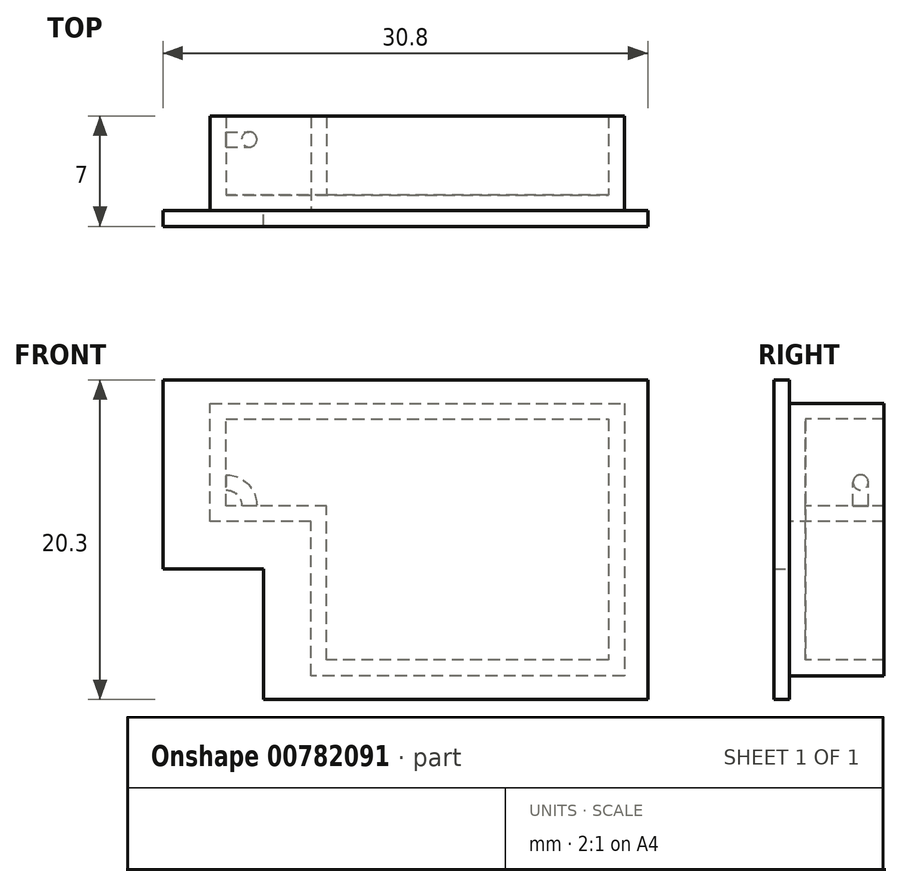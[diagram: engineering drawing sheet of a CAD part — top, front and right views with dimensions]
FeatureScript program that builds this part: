
annotation { "Feature Type Name" : "Feature", "Feature Type Description" : "" }
export const myFeature = defineFeature(function(context is Context, id is Id, definition is map)
    precondition{}
    {
        {
            var Q0;
            Q0=qCreatedBy(makeId("Front.planeOp"),FACE);
            var sketch = newSketch(context, id + "F0", { "sketchPlane" : qUnion([Q0])});
            skLineSegment(sketch, "E0", {"start": v(0, 0) * mm, "end": v(-19.9, 0) * mm});
            skLineSegment(sketch, "E1", {"start": v(-19.9, 0) * mm, "end": v(-19.9, 9.8) * mm});
            skLineSegment(sketch, "E2", {"start": v(-19.9, 9.8) * mm, "end": v(-26.3, 9.8) * mm});
            skLineSegment(sketch, "E3", {"start": v(-26.3, 9.8) * mm, "end": v(-26.3, 17.3) * mm});
            skLineSegment(sketch, "E4", {"start": v(-26.3, 17.3) * mm, "end": v(0, 17.3) * mm});
            skLineSegment(sketch, "E5", {"start": v(0, 17.3) * mm, "end": v(0, 0) * mm});
            skSolve(sketch);
        }
        {
            var Q0;
            Q0 = qSketchRegion(id + "F0", true);
            extrude(context, id + "F1", {"entities" : qUnion([Q0]), "oppositeDirection" : true, "depth" : 6 * mm, "offsetDistance" : 25 * mm});
        }
        {
            var Q0;
            Q0=makeQuery(id+"F1.opExtrude","CAP_FACE",FACE,{"disambiguationData":[OSD([sQuery(id+"F0.wireOp",EDGE,"E0"),sQuery(id+"F0.wireOp",EDGE,"E1"),sQuery(id+"F0.wireOp",EDGE,"E2"),sQuery(id+"F0.wireOp",EDGE,"E3"),sQuery(id+"F0.wireOp",EDGE,"E4"),sQuery(id+"F0.wireOp",EDGE,"E5")])],"isStart":false});
            shell(context, id + "F2", {"entities" : qUnion([Q0]), "thickness" : 1 * mm});
        }
        {
            var Q0;
            Q0=makeQuery(id+"F2.opShell","OFFSET_FACE",FACE,{"disambiguationData":[OSD([sQuery(id+"F0.wireOp",EDGE,"E2")])]});
            var sketch = newSketch(context, id + "F3", { "sketchPlane" : qUnion([Q0])});
            skCircle(sketch, "E6", {"center": v(-23.82, 4.52) * mm, "radius": 0.48 * mm});
            skLineSegment(sketch, "E7", {"start": v(-23.82, 5) * mm, "end": v(-23.82, 6) * mm, "construction": true});
            skLineSegment(sketch, "E8", {"start": v(-24.3, 4.52) * mm, "end": v(-25.3, 4.52) * mm, "construction": true});
            skSolve(sketch);
        }
        {
            var Q0;
            Q0 = qSketchRegion(id + "F3", true);
            var Q1;
            Q1=makeQuery(id+"F2.opShell","OFFSET_EDGE",EDGE,{"disambiguationData":[OSD([sQuery(id+"F0.wireOp",EDGE,"E2"),sQuery(id+"F0.wireOp",EDGE,"E3")])]});
            revolve(context, id + "F4", {"operationType" : NewBodyOperationType.ADD, "surfaceOperationType" : NewSurfaceOperationType.NEW, "entities" : qUnion([Q0]), "axis" : qUnion([Q1]), "revolveType" : RevolveType.ONE_DIRECTION, "angle" : 90 * degree});
        }
        {
            var Q0;
            Q0=makeQuery(id+"F1.opExtrude","CAP_FACE",FACE,{"disambiguationData":[OSD([sQuery(id+"F0.wireOp",EDGE,"E0"),sQuery(id+"F0.wireOp",EDGE,"E1"),sQuery(id+"F0.wireOp",EDGE,"E2"),sQuery(id+"F0.wireOp",EDGE,"E3"),sQuery(id+"F0.wireOp",EDGE,"E4"),sQuery(id+"F0.wireOp",EDGE,"E5")])],"isStart":true});
            var sketch = newSketch(context, id + "F5", { "sketchPlane" : qUnion([Q0])});
            skLineSegment(sketch, "E9", {"start": v(-26.3, 13.55) * mm, "end": v(-29.3, 13.55) * mm, "construction": true});
            skLineSegment(sketch, "E10", {"start": v(-13.15, 17.3) * mm, "end": v(-13.15, 18.8) * mm, "construction": true});
            skPoint(sketch, "E10.endSnap0", {"position": v(-13.15, 17.3) * mm});
            skLineSegment(sketch, "E11", {"start": v(0, 8.65) * mm, "end": v(1.5, 8.65) * mm, "construction": true});
            skPoint(sketch, "E11.endSnap0", {"position": v(0, 8.65) * mm});
            skLineSegment(sketch, "E12", {"start": v(-9.95, 0) * mm, "end": v(-9.95, -1.5) * mm, "construction": true});
            skPoint(sketch, "E12.endSnap0", {"position": v(-9.95, 0) * mm});
            skLineSegment(sketch, "E13", {"start": v(-19.9, 4.9) * mm, "end": v(-22.9, 4.9) * mm, "construction": true});
            skLineSegment(sketch, "E14", {"start": v(-25.21, 9.8) * mm, "end": v(-25.21, 6.8) * mm, "construction": true});
            skLineSegment(sketch, "E15", {"start": v(-29.3, 13.55) * mm, "end": v(-29.3, 18.8) * mm});
            skLineSegment(sketch, "E16", {"start": v(-29.3, 18.8) * mm, "end": v(1.5, 18.8) * mm});
            skLineSegment(sketch, "E17", {"start": v(1.5, 18.8) * mm, "end": v(1.5, -1.5) * mm});
            skLineSegment(sketch, "E18", {"start": v(1.5, -1.5) * mm, "end": v(-22.9, -1.5) * mm});
            skLineSegment(sketch, "E19", {"start": v(-22.9, -1.5) * mm, "end": v(-22.9, 4.9) * mm});
            skLineSegment(sketch, "E20", {"start": v(-22.9, 4.9) * mm, "end": v(-22.9, 6.8) * mm});
            skLineSegment(sketch, "E21", {"start": v(-22.9, 6.8) * mm, "end": v(-29.3, 6.8) * mm});
            skLineSegment(sketch, "E22", {"start": v(-29.3, 6.8) * mm, "end": v(-29.3, 13.55) * mm});
            skSolve(sketch);
        }
        {
            var Q0;
            Q0 = qSketchRegion(id + "F5", true);
            extrude(context, id + "F6", {"entities" : qUnion([Q0]), "operationType" : NewBodyOperationType.ADD, "depth" : 1 * mm, "offsetDistance" : 25 * mm});
        }
    });
